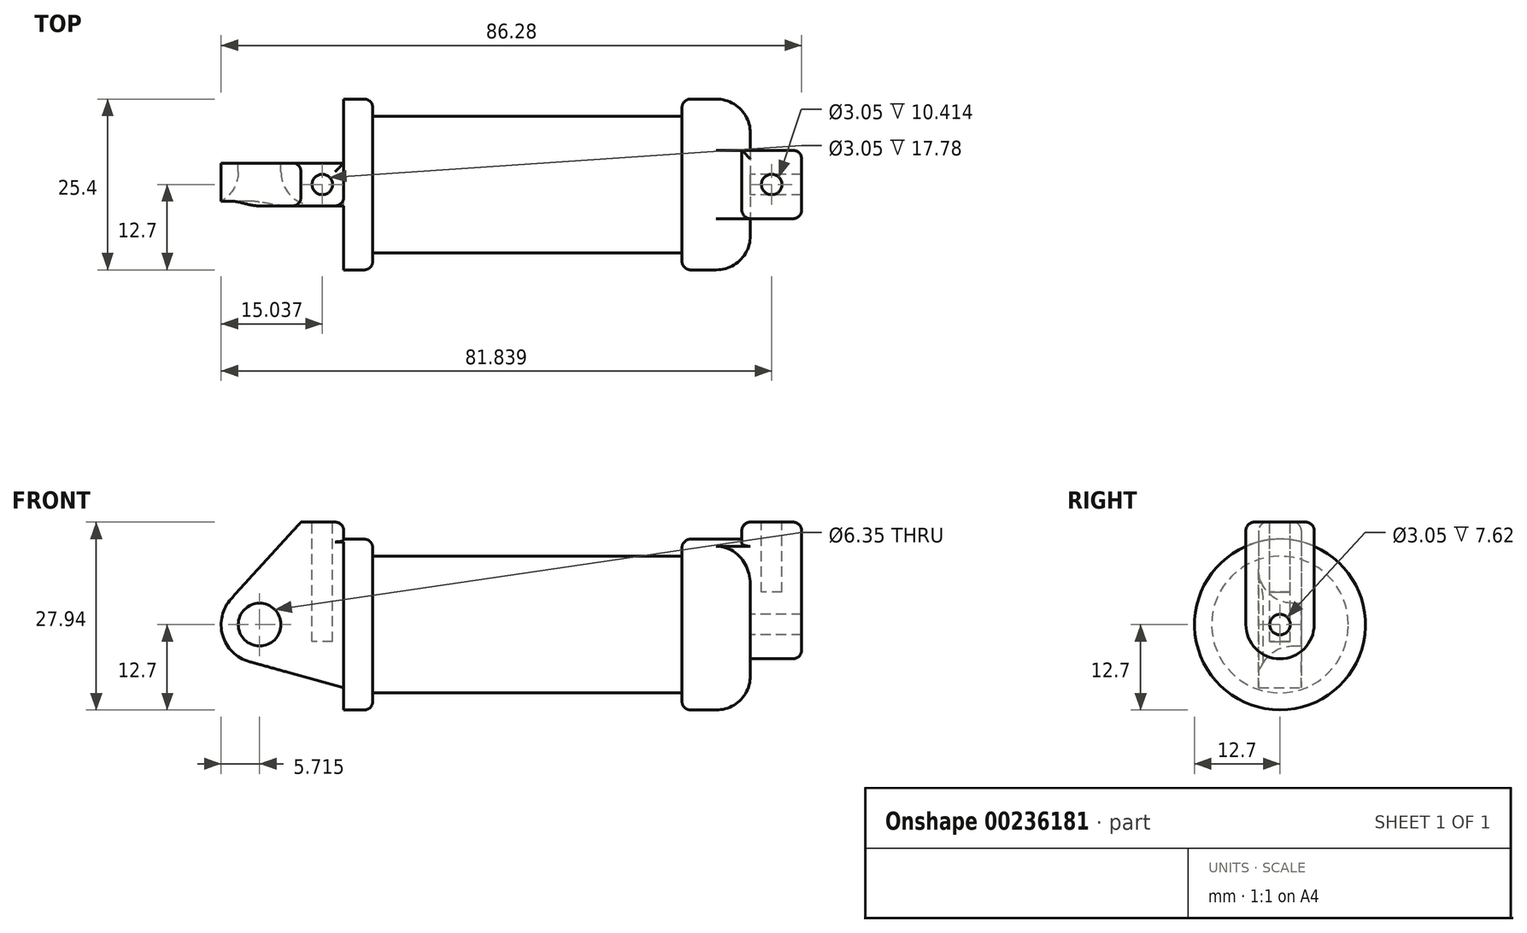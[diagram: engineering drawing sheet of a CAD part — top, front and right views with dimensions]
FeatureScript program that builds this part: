
annotation { "Feature Type Name" : "Feature", "Feature Type Description" : "" }
export const myFeature = defineFeature(function(context is Context, id is Id, definition is map)
    precondition{}
    {
        {
            var Q0;
            Q0=qCreatedBy(makeId("Front.planeOp"),FACE);
            var sketch = newSketch(context, id + "F0", { "sketchPlane" : qUnion([Q0])});
            skLineSegment(sketch, "E0", {"start": v(0, 0) * mm, "end": v(0, 12.7) * mm});
            skLineSegment(sketch, "E1", {"start": v(0, 12.7) * mm, "end": v(10.16, 12.7) * mm});
            skLineSegment(sketch, "E2", {"start": v(10.16, 12.7) * mm, "end": v(10.16, 10.16) * mm});
            skLineSegment(sketch, "E3", {"start": v(10.16, 10.16) * mm, "end": v(56.13, 10.16) * mm});
            skLineSegment(sketch, "E4", {"start": v(56.13, 10.16) * mm, "end": v(56.13, 12.7) * mm});
            skLineSegment(sketch, "E5", {"start": v(56.13, 12.7) * mm, "end": v(66.3, 12.7) * mm});
            skLineSegment(sketch, "E6", {"start": v(66.3, 12.7) * mm, "end": v(66.3, 0) * mm});
            skLineSegment(sketch, "E7", {"start": v(66.3, 0) * mm, "end": v(0, 0) * mm});
            skLineSegment(sketch, "E8", {"start": v(5.84, 15.24) * mm, "end": v(-0.5, 15.24) * mm});
            skLineSegment(sketch, "E9", {"start": v(-0.5, 15.24) * mm, "end": v(-10.88, 3.85) * mm});
            skLineSegment(sketch, "E10", {"start": v(0, 0) * mm, "end": v(-6.65, 0) * mm});
            skCircle(sketch, "E11", {"center": v(-6.65, 0) * mm, "radius": 5.72 * mm});
            skCircle(sketch, "E12", {"center": v(-6.65, 0) * mm, "radius": 3.18 * mm});
            skLineSegment(sketch, "E13", {"start": v(5.84, 15.24) * mm, "end": v(5.84, -9.4) * mm});
            skLineSegment(sketch, "E14", {"start": v(5.84, -9.4) * mm, "end": v(-8.18, -5.5) * mm});
            skSolve(sketch);
        }
        {
            var Q0;
            {var subQ0=sQuery(id+"F0.wireOp",EDGE,"E2");Q0=makeQuery(id+"F0.imprint","IMPRINT",FACE,{"disambiguationData":[TD([[makeQuery(id+"F0.imprint","IMPRINT",EDGE,{"derivedFrom":subQ0}),-1.0]])]});}
            var Q1;
            Q1=sQuery(id+"F0.wireOp",EDGE,"E7");
            revolve(context, id + "F1", {"entities" : qUnion([Q0]), "axis" : qUnion([Q1]), "revolveType" : RevolveType.FULL});
        }
        {
            var Q0;
            {var subQ0=sQuery(id+"F0.wireOp",EDGE,"E0");Q0=makeQuery(id+"F0.imprint","IMPRINT",FACE,{"disambiguationData":[TD([[makeQuery(id+"F0.imprint","IMPRINT",EDGE,{"derivedFrom":subQ0}),-1.0]])]});}
            var Q1;
            {var subQ3=sQuery(id+"F0.wireOp",EDGE,"E0");Q1=makeQuery(id+"F0.imprint","IMPRINT",FACE,{"disambiguationData":[TD([[makeQuery(id+"F0.imprint","IMPRINT",EDGE,{"derivedFrom":subQ3}),1.0]])]});}
            var Q2;
            {var subQ4=sQuery(id+"F0.wireOp",EDGE,"E12");Q2=makeQuery(id+"F0.imprint","IMPRINT",FACE,{"disambiguationData":[TD([[makeQuery(id+"F0.imprint","IMPRINT",EDGE,{"derivedFrom":subQ4}),-1.0]])]});}
            var Q3;
            {var subQ0=sQuery(id+"F0.wireOp",EDGE,"E14");Q3=makeQuery(id+"F0.imprint","IMPRINT",FACE,{"disambiguationData":[TD([[makeQuery(id+"F0.imprint","IMPRINT",EDGE,{"derivedFrom":subQ0}),-1.0]])]});}
            extrude(context, id + "F2", {"entities" : qUnion([Q0, Q1, Q2, Q3]), "operationType" : NewBodyOperationType.ADD, "endBound" : BoundingType.SYMMETRIC, "depth" : 6.35 * mm});
        }
        {
            var Q0;
            Q0=makeQuery(id+"F1.opRevolve","SWEPT_FACE",FACE,{"disambiguationData":[OSD([sQuery(id+"F0.wireOp",EDGE,"E6")])]});
            var sketch = newSketch(context, id + "F3", { "sketchPlane" : qUnion([Q0])});
            skCircle(sketch, "E15", {"center": v(0, 0) * mm, "radius": 1.52 * mm});
            skCircle(sketch, "E16", {"center": v(0, 0) * mm, "radius": 5.08 * mm});
            skLineSegment(sketch, "E17", {"start": v(5.08, 0) * mm, "end": v(5.08, 15.24) * mm});
            skLineSegment(sketch, "E18", {"start": v(-5.08, 0) * mm, "end": v(-5.08, 15.24) * mm});
            skLineSegment(sketch, "E19", {"start": v(-5.08, 15.24) * mm, "end": v(5.08, 15.24) * mm});
            skSolve(sketch);
        }
        {
            var Q0;
            {var subQ0=sQuery(id+"F3.wireOp",EDGE,"E19");Q0=makeQuery(id+"F3.imprint","IMPRINT",FACE,{"disambiguationData":[TD([[makeQuery(id+"F3.imprint","IMPRINT",EDGE,{"derivedFrom":subQ0}),-1.0]])]});}
            var Q1;
            {var subQ0=sQuery(id+"F3.wireOp",EDGE,"E17");var subQ1=sQuery(id+"F3.wireOp",EDGE,"E16");var subQ2=makeQuery(id+"F3.imprint","INTERSECT",VERTEX,{"derivedFrom":[subQ1,subQ0]});Q1=makeQuery(id+"F3.imprint","IMPRINT",FACE,{"disambiguationData":[TD([[makeQuery(id+"F3.imprint","IMPRINT",EDGE,{"disambiguationData":[TD([[subQ2,-1.0]])],"derivedFrom":subQ1}),-1.0]])]});}
            var Q2;
            Q2=makeQuery(id+"F3.imprint","IMPRINT",FACE,{"disambiguationData":[TD([[makeQuery(id+"F3.imprint","IMPRINT",EDGE,{"derivedFrom":sQuery(id+"F3.wireOp",EDGE,"E15")}),-1.0]])]});
            extrude(context, id + "F4", {"entities" : qUnion([Q0, Q1, Q2]), "operationType" : NewBodyOperationType.ADD, "depth" : 7.62 * mm});
        }
        {
            var Q0;
            {var subQ0=sQuery(id+"F3.wireOp",EDGE,"E19");Q0=makeQuery(id+"F3.imprint","IMPRINT",FACE,{"disambiguationData":[TD([[makeQuery(id+"F3.imprint","IMPRINT",EDGE,{"derivedFrom":subQ0}),-1.0]])]});}
            var Q1;
            {var subQ0=sQuery(id+"F3.wireOp",EDGE,"E17");var subQ1=sQuery(id+"F3.wireOp",EDGE,"E16");var subQ2=makeQuery(id+"F3.imprint","INTERSECT",VERTEX,{"derivedFrom":[subQ1,subQ0]});Q1=makeQuery(id+"F3.imprint","IMPRINT",FACE,{"disambiguationData":[TD([[makeQuery(id+"F3.imprint","IMPRINT",EDGE,{"disambiguationData":[TD([[subQ2,-1.0]])],"derivedFrom":subQ1}),-1.0]])]});}
            var Q2;
            Q2=makeQuery(id+"F3.imprint","IMPRINT",FACE,{"disambiguationData":[TD([[makeQuery(id+"F3.imprint","IMPRINT",EDGE,{"derivedFrom":sQuery(id+"F3.wireOp",EDGE,"E15")}),-1.0]])]});
            extrude(context, id + "F5", {"entities" : qUnion([Q0, Q1, Q2]), "operationType" : NewBodyOperationType.ADD, "oppositeDirection" : true, "depth" : 1.27 * mm});
        }
        {
            var Q0;
            Q0=makeQuery(id+"F2.opExtrude","SWEPT_FACE",FACE,{"disambiguationData":[OSD([sQuery(id+"F0.wireOp",EDGE,"E8")])]});
            var sketch = newSketch(context, id + "F6", { "sketchPlane" : qUnion([Q0])});
            skCircle(sketch, "E20", {"center": v(2.67, 0) * mm, "radius": 1.52 * mm});
            skSolve(sketch);
        }
        {
            var Q0;
            {var subQ0=sQuery(id+"F3.wireOp",EDGE,"E19");Q0=makeQuery(id+"F5.boolean.opBoolean","MERGE",FACE,{"derivedFrom":[makeQuery(id+"F4.opExtrude","SWEPT_FACE",FACE,{"disambiguationData":[OSD([subQ0])]}),makeQuery(id+"F5.opExtrude","SWEPT_FACE",FACE,{"disambiguationData":[OSD([subQ0])]})]});}
            var sketch = newSketch(context, id + "F7", { "sketchPlane" : qUnion([Q0])});
            skCircle(sketch, "E21", {"center": v(69.47, 0) * mm, "radius": 1.52 * mm});
            skSolve(sketch);
        }
        {
            var Q0;
            Q0 = qSketchRegion(id + "F7", true);
            extrude(context, id + "F8", {"entities" : qUnion([Q0]), "operationType" : NewBodyOperationType.REMOVE, "oppositeDirection" : true, "depth" : 10.4 * mm});
        }
        {
            var Q0;
            Q0 = qSketchRegion(id + "F6", true);
            extrude(context, id + "F9", {"entities" : qUnion([Q0]), "operationType" : NewBodyOperationType.REMOVE, "oppositeDirection" : true, "depth" : 17.78 * mm});
        }
        {
            var Q0;
            Q0=makeQuery(id+"F1.opRevolve","SWEPT_EDGE",EDGE,{"disambiguationData":[OSD([sQuery(id+"F0.wireOp",EDGE,"E1"),sQuery(id+"F0.wireOp",EDGE,"E2")])]});
            fillet(context, id + "F10", {"entities" : qUnion([Q0]), "radius" : 1.27 * mm, "tangentPropagation" : true, "allowEdgeOverflow" : false});
        }
        {
            var Q0;
            Q0=makeQuery(id+"F1.opRevolve","SWEPT_EDGE",EDGE,{"disambiguationData":[OSD([sQuery(id+"F0.wireOp",EDGE,"E4"),sQuery(id+"F0.wireOp",EDGE,"E5")])]});
            var Q1;
            {var subQ0=sQuery(id+"F3.wireOp",EDGE,"E19");var subQ1=sQuery(id+"F3.wireOp",EDGE,"E18");Q1=makeQuery(id+"F5.boolean.opBoolean","MERGE",EDGE,{"derivedFrom":[makeQuery(id+"F4.opExtrude","SWEPT_EDGE",EDGE,{"disambiguationData":[OSD([subQ1,subQ0])]}),makeQuery(id+"F5.opExtrude","SWEPT_EDGE",EDGE,{"disambiguationData":[OSD([subQ1,subQ0])]})]});}
            fillet(context, id + "F11", {"entities" : qUnion([Q0, Q1]), "radius" : 1.27 * mm, "tangentPropagation" : true, "allowEdgeOverflow" : false});
        }
        {
            var Q0;
            Q0=makeQuery(id+"F4.opExtrude","CAP_EDGE",EDGE,{"disambiguationData":[OSD([sQuery(id+"F3.wireOp",EDGE,"E19")])],"isStart":false});
            fillet(context, id + "F12", {"entities" : qUnion([Q0]), "radius" : 1.27 * mm, "tangentPropagation" : true, "allowEdgeOverflow" : false});
        }
        {
            var Q0;
            Q0=makeQuery(id+"F5.opExtrude","CAP_EDGE",EDGE,{"disambiguationData":[OSD([sQuery(id+"F3.wireOp",EDGE,"E19")])],"isStart":false});
            var Q1;
            {var subQ0=sQuery(id+"F3.wireOp",EDGE,"E19");var subQ1=sQuery(id+"F3.wireOp",EDGE,"E17");Q1=makeQuery(id+"F5.boolean.opBoolean","MERGE",EDGE,{"derivedFrom":[makeQuery(id+"F4.opExtrude","SWEPT_EDGE",EDGE,{"disambiguationData":[OSD([subQ1,subQ0])]}),makeQuery(id+"F5.opExtrude","SWEPT_EDGE",EDGE,{"disambiguationData":[OSD([subQ1,subQ0])]})]});}
            fillet(context, id + "F13", {"entities" : qUnion([Q0, Q1]), "radius" : 1.27 * mm, "tangentPropagation" : true, "allowEdgeOverflow" : false});
        }
        {
            var Q0;
            Q0=makeQuery(id+"F4.boolean.opBoolean","SPLIT",EDGE,{"disambiguationData":[OD(1.0)],"derivedFrom":makeQuery(id+"F1.opRevolve","SWEPT_EDGE",EDGE,{"disambiguationData":[OSD([sQuery(id+"F0.wireOp",EDGE,"E5"),sQuery(id+"F0.wireOp",EDGE,"E6")])]})});
            var Q1;
            Q1=makeQuery(id+"F2.opExtrude","CAP_EDGE",EDGE,{"disambiguationData":[OSD([sQuery(id+"F0.wireOp",EDGE,"E12")])],"isStart":false});
            fillet(context, id + "F14", {"entities" : qUnion([Q0, Q1]), "radius" : 5.08 * mm, "tangentPropagation" : true, "allowEdgeOverflow" : false});
        }
        {
            var Q0;
            Q0=makeQuery(id+"F2.opExtrude","SWEPT_EDGE",EDGE,{"disambiguationData":[OSD([sQuery(id+"F0.wireOp",EDGE,"E8"),sQuery(id+"F0.wireOp",EDGE,"E13")])]});
            var Q1;
            Q1=makeQuery(id+"F2.opExtrude","CAP_EDGE",EDGE,{"disambiguationData":[OSD([sQuery(id+"F0.wireOp",EDGE,"E8")])],"isStart":true});
            fillet(context, id + "F15", {"entities" : qUnion([Q0, Q1]), "radius" : 1.27 * mm, "tangentPropagation" : true, "allowEdgeOverflow" : false});
        }
        {
            var Q0;
            Q0=makeQuery(id+"F2.opExtrude","CAP_EDGE",EDGE,{"disambiguationData":[OSD([sQuery(id+"F0.wireOp",EDGE,"E8")])],"isStart":false});
            fillet(context, id + "F16", {"entities" : qUnion([Q0]), "radius" : 1.27 * mm, "tangentPropagation" : true, "allowEdgeOverflow" : false});
        }
    });
